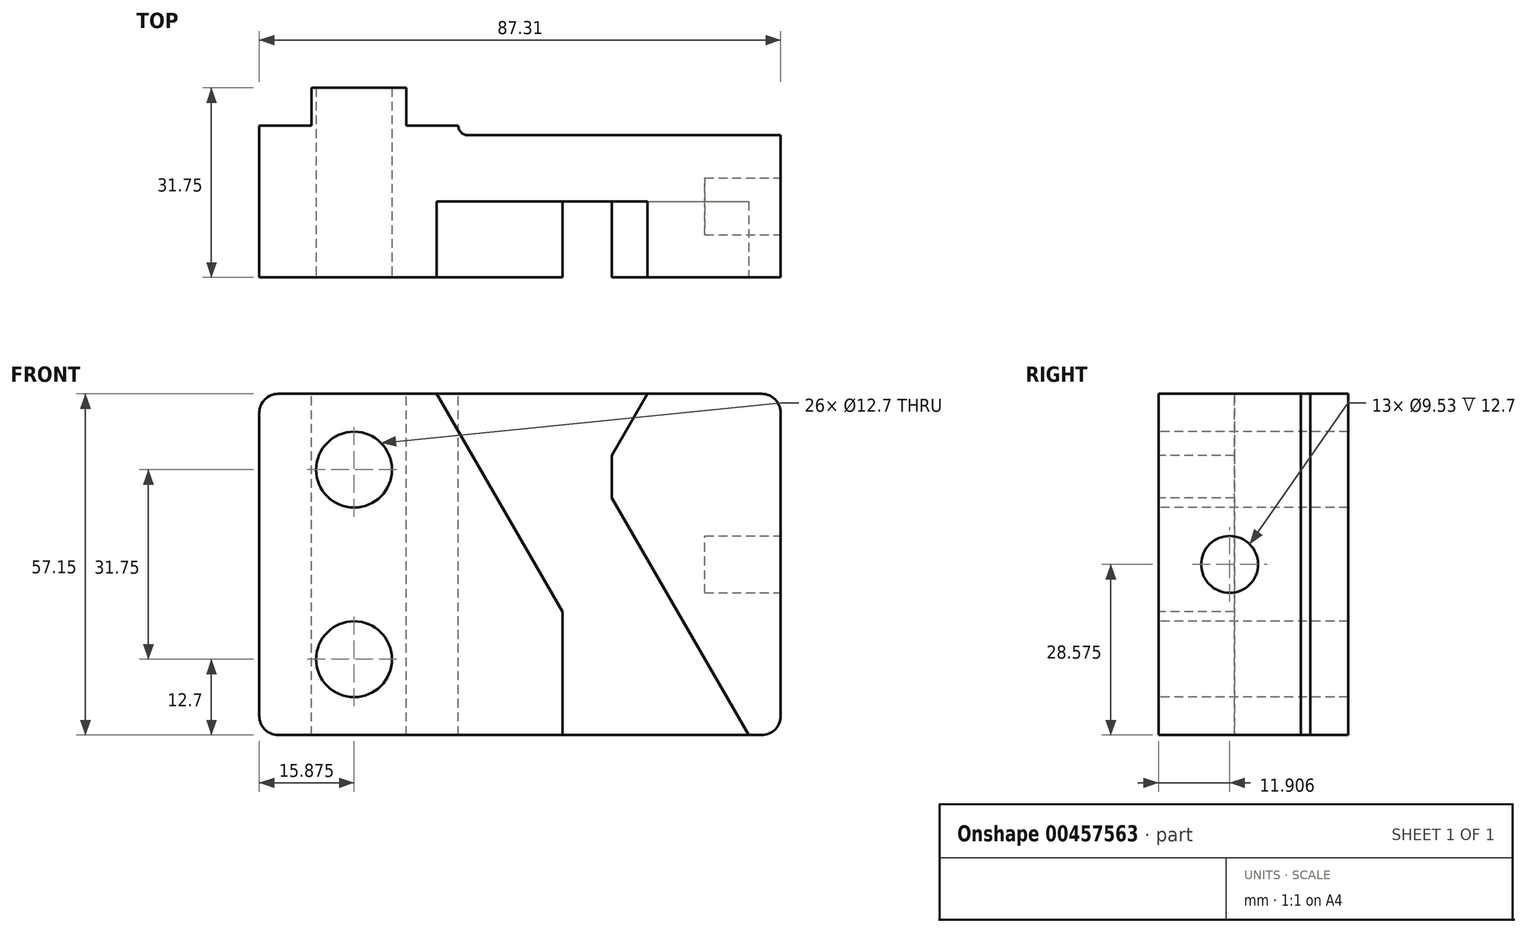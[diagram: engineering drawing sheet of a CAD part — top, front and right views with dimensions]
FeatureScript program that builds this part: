
annotation { "Feature Type Name" : "Feature", "Feature Type Description" : "" }
export const myFeature = defineFeature(function(context is Context, id is Id, definition is map)
    precondition{}
    {
        {
            var Q0;
            Q0=qCreatedBy(makeId("Front.planeOp"),FACE);
            var sketch = newSketch(context, id + "F0", { "sketchPlane" : qUnion([Q0])});
            skLineSegment(sketch, "E0.bottom", {"start": v(0, 0) * mm, "end": v(87.31, 0) * mm});
            skLineSegment(sketch, "E0.top", {"start": v(0, -57.15) * mm, "end": v(87.31, -57.15) * mm});
            skLineSegment(sketch, "E0.left", {"start": v(0, 0) * mm, "end": v(0, -57.15) * mm});
            skLineSegment(sketch, "E0.right", {"start": v(87.31, 0) * mm, "end": v(87.31, -57.15) * mm});
            skSolve(sketch);
        }
        {
            var Q0;
            Q0=makeQuery(id+"F0.imprint","IMPRINT",FACE,{"disambiguationData":[TD([[makeQuery(id+"F0.imprint","IMPRINT",EDGE,{"derivedFrom":sQuery(id+"F0.wireOp",EDGE,"E0.bottom")}),-1.0]])]});
            extrude(context, id + "F1", {"entities" : qUnion([Q0]), "depth" : 31.75 * mm});
        }
        {
            var Q0;
            Q0=makeQuery(id+"F1.opExtrude","CAP_FACE",FACE,{"disambiguationData":[OSD([sQuery(id+"F0.wireOp",EDGE,"E0.bottom"),sQuery(id+"F0.wireOp",EDGE,"E0.top"),sQuery(id+"F0.wireOp",EDGE,"E0.left"),sQuery(id+"F0.wireOp",EDGE,"E0.right")])],"isStart":false});
            var sketch = newSketch(context, id + "F2", { "sketchPlane" : qUnion([Q0])});
            skLineSegment(sketch, "E1", {"start": v(50.8, -57.15) * mm, "end": v(50.8, -36.51) * mm});
            skLineSegment(sketch, "E2", {"start": v(50.8, -36.51) * mm, "end": v(29.72, 0) * mm});
            skLineSegment(sketch, "E3", {"start": v(29.72, 0) * mm, "end": v(65, 0) * mm});
            skLineSegment(sketch, "E4", {"start": v(65, 0) * mm, "end": v(59.05, -10.32) * mm});
            skLineSegment(sketch, "E5", {"start": v(59.05, -10.32) * mm, "end": v(59.05, -17.46) * mm});
            skLineSegment(sketch, "E6", {"start": v(59.05, -17.46) * mm, "end": v(81.96, -57.15) * mm});
            skLineSegment(sketch, "E7", {"start": v(50.8, -57.15) * mm, "end": v(81.96, -57.15) * mm});
            skSolve(sketch);
        }
        {
            var Q0;
            Q0=makeQuery(id+"F2.imprint","IMPRINT",FACE,{"disambiguationData":[TD([[makeQuery(id+"F2.imprint","IMPRINT",EDGE,{"derivedFrom":sQuery(id+"F2.wireOp",EDGE,"E1")}),-1.0]])]});
            extrude(context, id + "F3", {"entities" : qUnion([Q0]), "operationType" : NewBodyOperationType.REMOVE, "oppositeDirection" : true, "depth" : 12.7 * mm});
        }
        {
            var Q0;
            Q0=makeQuery(id+"F1.opExtrude","SWEPT_FACE",FACE,{"disambiguationData":[OSD([sQuery(id+"F0.wireOp",EDGE,"E0.bottom")])]});
            var sketch = newSketch(context, id + "F4", { "sketchPlane" : qUnion([Q0])});
            skLineSegment(sketch, "E8", {"start": v(0, -6.35) * mm, "end": v(8.73, -6.35) * mm});
            skLineSegment(sketch, "E9", {"start": v(8.73, -6.35) * mm, "end": v(8.73, 0) * mm});
            skLineSegment(sketch, "E10", {"start": v(24.6, 0) * mm, "end": v(24.6, -6.35) * mm});
            skLineSegment(sketch, "E11", {"start": v(24.6, -6.35) * mm, "end": v(33.34, -6.35) * mm});
            skLineSegment(sketch, "E12", {"start": v(33.34, -6.35) * mm, "end": v(33.34, -7.94) * mm});
            skLineSegment(sketch, "E13", {"start": v(33.34, -7.94) * mm, "end": v(87.31, -7.94) * mm});
            skLineSegment(sketch, "E14", {"start": v(87.31, -7.94) * mm, "end": v(87.31, 0) * mm});
            skLineSegment(sketch, "E15", {"start": v(87.31, 0) * mm, "end": v(24.6, 0) * mm});
            skLineSegment(sketch, "E16", {"start": v(0, 0) * mm, "end": v(8.73, 0) * mm});
            skLineSegment(sketch, "E17", {"start": v(0, 0) * mm, "end": v(0, -6.35) * mm});
            skSolve(sketch);
        }
        {
            var Q0;
            Q0=makeQuery(id+"F4.imprint","IMPRINT",FACE,{"disambiguationData":[TD([[makeQuery(id+"F4.imprint","IMPRINT",EDGE,{"derivedFrom":sQuery(id+"F4.wireOp",EDGE,"E10")}),1.0]])]});
            var Q1;
            Q1=makeQuery(id+"F4.imprint","IMPRINT",FACE,{"disambiguationData":[TD([[makeQuery(id+"F4.imprint","IMPRINT",EDGE,{"derivedFrom":sQuery(id+"F4.wireOp",EDGE,"E8")}),1.0]])]});
            extrude(context, id + "F5", {"entities" : qUnion([Q0, Q1]), "operationType" : NewBodyOperationType.REMOVE, "oppositeDirection" : true, "depth" : 66.3 * mm});
        }
        {
            var Q0;
            Q0=makeQuery(id+"F5.boolean.opBoolean","COPY",EDGE,{"derivedFrom":makeQuery(id+"F5.opExtrude","SWEPT_EDGE",EDGE,{"disambiguationData":[OSD([sQuery(id+"F4.wireOp",EDGE,"E12"),sQuery(id+"F4.wireOp",EDGE,"E13")])]})});
            fillet(context, id + "F6", {"entities" : qUnion([Q0]), "radius" : 1.59 * mm, "tangentPropagation" : true, "allowEdgeOverflow" : false});
        }
        {
            var Q0;
            Q0=makeQuery(id+"F1.opExtrude","SWEPT_EDGE",EDGE,{"disambiguationData":[OSD([sQuery(id+"F0.wireOp",EDGE,"E0.bottom"),sQuery(id+"F0.wireOp",EDGE,"E0.right")])]});
            var Q1;
            Q1=makeQuery(id+"F1.opExtrude","SWEPT_EDGE",EDGE,{"disambiguationData":[OSD([sQuery(id+"F0.wireOp",EDGE,"E0.bottom"),sQuery(id+"F0.wireOp",EDGE,"E0.left")])]});
            var Q2;
            Q2=makeQuery(id+"F1.opExtrude","SWEPT_EDGE",EDGE,{"disambiguationData":[OSD([sQuery(id+"F0.wireOp",EDGE,"E0.top"),sQuery(id+"F0.wireOp",EDGE,"E0.right")])]});
            var Q3;
            Q3=makeQuery(id+"F1.opExtrude","SWEPT_EDGE",EDGE,{"disambiguationData":[OSD([sQuery(id+"F0.wireOp",EDGE,"E0.top"),sQuery(id+"F0.wireOp",EDGE,"E0.left")])]});
            fillet(context, id + "F7", {"entities" : qUnion([Q0, Q1, Q2, Q3]), "radius" : 3.17 * mm, "tangentPropagation" : true, "allowEdgeOverflow" : false});
        }
        {
            var Q0;
            {var subQ0=sQuery(id+"F0.wireOp",EDGE,"E0.left");var subQ1=sQuery(id+"F0.wireOp",EDGE,"E0.top");var subQ2=sQuery(id+"F0.wireOp",EDGE,"E0.bottom");Q0=makeQuery(id+"F3.boolean.opBoolean","SPLIT",FACE,{"disambiguationData":[TD([makeQuery(id+"F1.opExtrude","SWEPT_FACE",FACE,{"disambiguationData":[OSD([subQ0])]})])],"derivedFrom":makeQuery(id+"F1.opExtrude","CAP_FACE",FACE,{"disambiguationData":[OSD([subQ2,subQ1,subQ0,sQuery(id+"F0.wireOp",EDGE,"E0.right")])],"isStart":false})});}
            var sketch = newSketch(context, id + "F8", { "sketchPlane" : qUnion([Q0])});
            skCircle(sketch, "E18", {"center": v(15.88, -12.7) * mm, "radius": 6.35 * mm});
            skCircle(sketch, "E19", {"center": v(15.88, -44.45) * mm, "radius": 6.35 * mm});
            skSolve(sketch);
        }
        {
            var Q0;
            Q0=makeQuery(id+"F8.imprint","IMPRINT",FACE,{"disambiguationData":[TD([[makeQuery(id+"F8.imprint","IMPRINT",EDGE,{"derivedFrom":sQuery(id+"F8.wireOp",EDGE,"E18")}),1.0]])]});
            var Q1;
            Q1=makeQuery(id+"F8.imprint","IMPRINT",FACE,{"disambiguationData":[TD([[makeQuery(id+"F8.imprint","IMPRINT",EDGE,{"derivedFrom":sQuery(id+"F8.wireOp",EDGE,"E19")}),1.0]])]});
            extrude(context, id + "F9", {"entities" : qUnion([Q0, Q1]), "operationType" : NewBodyOperationType.REMOVE, "oppositeDirection" : true, "depth" : 108.2 * mm});
        }
        {
            var Q0;
            Q0=makeQuery(id+"F1.opExtrude","SWEPT_FACE",FACE,{"disambiguationData":[OSD([sQuery(id+"F0.wireOp",EDGE,"E0.right")])]});
            var sketch = newSketch(context, id + "F10", { "sketchPlane" : qUnion([Q0])});
            skCircle(sketch, "E20", {"center": v(-19.84, -28.58) * mm, "radius": 4.76 * mm});
            skSolve(sketch);
        }
        {
            var Q0;
            Q0=makeQuery(id+"F10.imprint","IMPRINT",FACE,{"disambiguationData":[TD([[makeQuery(id+"F10.imprint","IMPRINT",EDGE,{"derivedFrom":sQuery(id+"F10.wireOp",EDGE,"E20")}),1.0]])]});
            extrude(context, id + "F11", {"entities" : qUnion([Q0]), "operationType" : NewBodyOperationType.REMOVE, "oppositeDirection" : true, "depth" : 12.7 * mm});
        }
    });
